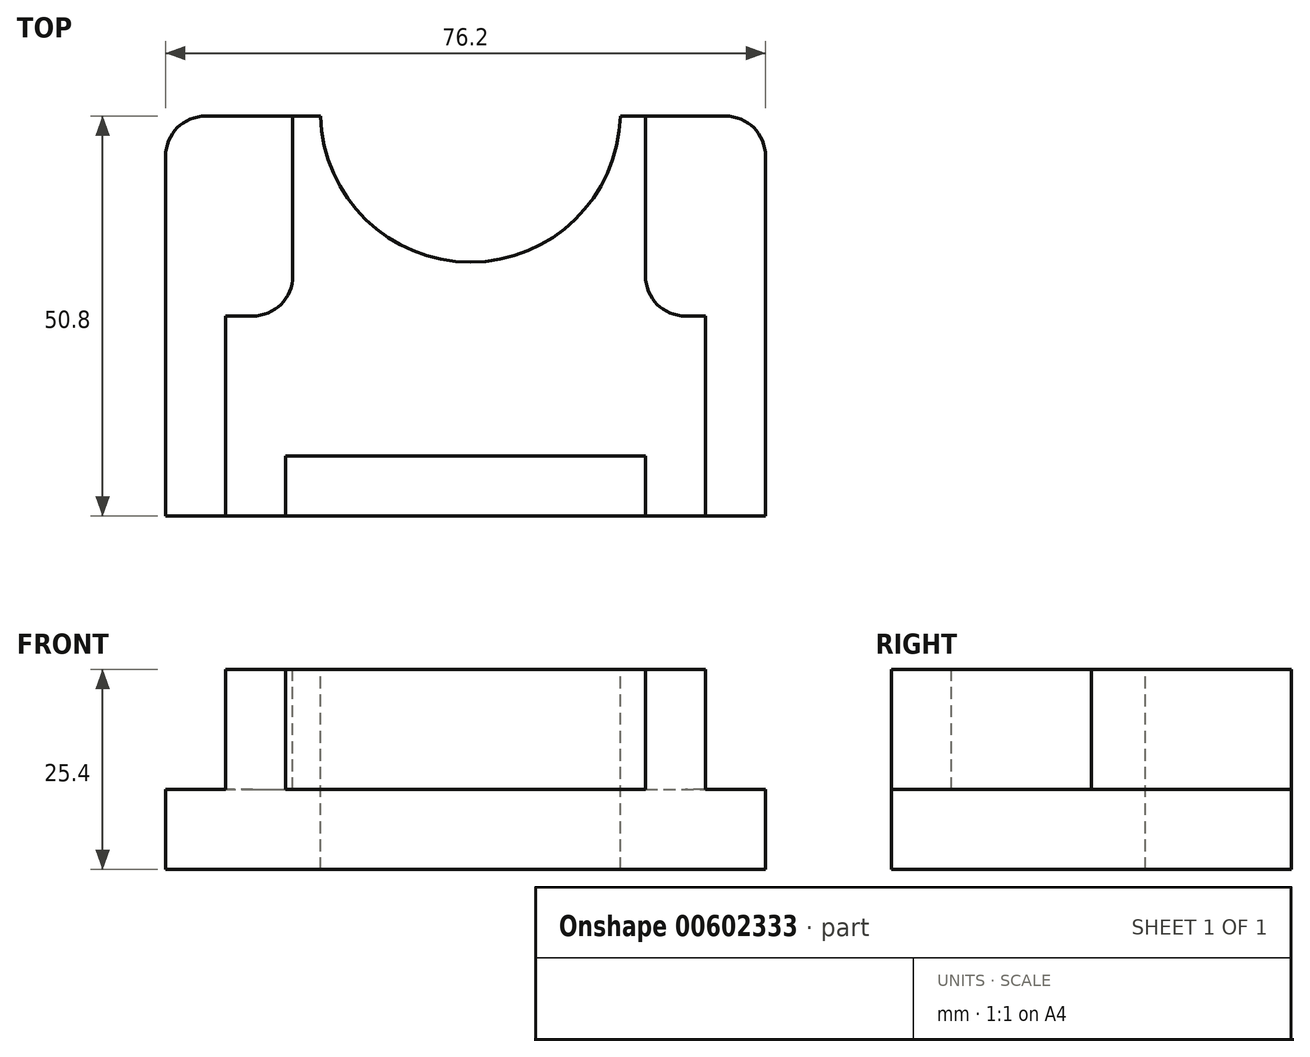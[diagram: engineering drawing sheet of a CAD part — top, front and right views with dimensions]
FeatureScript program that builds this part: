
annotation { "Feature Type Name" : "Feature", "Feature Type Description" : "" }
export const myFeature = defineFeature(function(context is Context, id is Id, definition is map)
    precondition{}
    {
        {
            var Q0;
            Q0=qCreatedBy(makeId("Top.planeOp"),FACE);
            var sketch = newSketch(context, id + "F0", { "sketchPlane" : qUnion([Q0])});
            skLineSegment(sketch, "E0.bottom", {"start": v(-50.23, 50.8) * mm, "end": v(25.97, 50.8) * mm});
            skLineSegment(sketch, "E0.top", {"start": v(-50.23, 0) * mm, "end": v(25.97, 0) * mm});
            skLineSegment(sketch, "E0.left", {"start": v(-50.23, 50.8) * mm, "end": v(-50.23, 0) * mm});
            skLineSegment(sketch, "E0.right", {"start": v(25.97, 50.8) * mm, "end": v(25.97, 0) * mm});
            skSolve(sketch);
        }
        {
            var Q0;
            Q0=makeQuery(id+"F0.imprint","IMPRINT",FACE,{"disambiguationData":[TD([[makeQuery(id+"F0.imprint","IMPRINT",EDGE,{"derivedFrom":sQuery(id+"F0.wireOp",EDGE,"E0.bottom")}),-1.0]])]});
            extrude(context, id + "F1", {"entities" : qUnion([Q0]), "depth" : 10.16 * mm, "offsetDistance" : 25.4 * mm});
        }
        {
            var Q0;
            Q0=qCreatedBy(makeId("Top.planeOp"),FACE);
            var sketch = newSketch(context, id + "F2", { "sketchPlane" : qUnion([Q0])});
            skLineSegment(sketch, "E1.bottom", {"start": v(-42.61, 50.8) * mm, "end": v(18.35, 50.8) * mm});
            skLineSegment(sketch, "E1.top", {"start": v(-42.61, 0) * mm, "end": v(18.35, 0) * mm});
            skLineSegment(sketch, "E1.left", {"start": v(-42.61, 50.8) * mm, "end": v(-42.61, 0) * mm});
            skLineSegment(sketch, "E1.right", {"start": v(18.35, 50.8) * mm, "end": v(18.35, 0) * mm});
            skSolve(sketch);
        }
        {
            var Q0;
            Q0 = qSketchRegion(id + "F2", true);
            extrude(context, id + "F3", {"entities" : qUnion([Q0]), "operationType" : NewBodyOperationType.ADD, "depth" : 25.4 * mm, "offsetDistance" : 25.4 * mm});
        }
        {
            var Q0;
            Q0=makeQuery(id+"F3.opExtrude","CAP_FACE",FACE,{"disambiguationData":[OSD([sQuery(id+"F2.wireOp",EDGE,"E1.bottom"),sQuery(id+"F2.wireOp",EDGE,"E1.top"),sQuery(id+"F2.wireOp",EDGE,"E1.left"),sQuery(id+"F2.wireOp",EDGE,"E1.right")])],"isStart":false});
            var sketch = newSketch(context, id + "F4", { "sketchPlane" : qUnion([Q0])});
            skLineSegment(sketch, "E2.bottom", {"start": v(-35, 7.62) * mm, "end": v(10.73, 7.62) * mm});
            skLineSegment(sketch, "E2.top", {"start": v(-35, 0) * mm, "end": v(10.73, 0) * mm});
            skLineSegment(sketch, "E2.left", {"start": v(-35, 7.62) * mm, "end": v(-35, 0) * mm});
            skLineSegment(sketch, "E2.right", {"start": v(10.73, 7.62) * mm, "end": v(10.73, 0) * mm});
            skCircle(sketch, "E3", {"center": v(-11.51, 51.3) * mm, "radius": 19.05 * mm});
            skLineSegment(sketch, "E4.bottom", {"start": v(-42.61, 25.4) * mm, "end": v(-34.1, 25.4) * mm});
            skLineSegment(sketch, "E4.top", {"start": v(-42.61, 50.8) * mm, "end": v(-34.1, 50.8) * mm});
            skLineSegment(sketch, "E4.left", {"start": v(-42.61, 25.4) * mm, "end": v(-42.61, 50.8) * mm});
            skLineSegment(sketch, "E4.right", {"start": v(-34.1, 25.4) * mm, "end": v(-34.1, 50.8) * mm});
            skLineSegment(sketch, "E5.bottom", {"start": v(10.73, 25.4) * mm, "end": v(18.35, 25.4) * mm});
            skLineSegment(sketch, "E5.top", {"start": v(10.73, 50.8) * mm, "end": v(18.35, 50.8) * mm});
            skLineSegment(sketch, "E5.left", {"start": v(10.73, 25.4) * mm, "end": v(10.73, 50.8) * mm});
            skLineSegment(sketch, "E5.right", {"start": v(18.35, 25.4) * mm, "end": v(18.35, 50.8) * mm});
            skSolve(sketch);
        }
        {
            var Q0;
            Q0=makeQuery(id+"F4.imprint","IMPRINT",FACE,{"disambiguationData":[TD([[makeQuery(id+"F4.imprint","IMPRINT",EDGE,{"derivedFrom":sQuery(id+"F4.wireOp",EDGE,"E3")}),1.0]])]});
            extrude(context, id + "F5", {"entities" : qUnion([Q0]), "operationType" : NewBodyOperationType.REMOVE, "endBound" : BoundingType.THROUGH_ALL, "oppositeDirection" : true, "depth" : 25.4 * mm, "offsetDistance" : 25.4 * mm});
        }
        {
            var Q0;
            Q0=makeQuery(id+"F4.imprint","IMPRINT",FACE,{"disambiguationData":[TD([[makeQuery(id+"F4.imprint","IMPRINT",EDGE,{"derivedFrom":sQuery(id+"F4.wireOp",EDGE,"E4.bottom")}),1.0]])]});
            var Q1;
            Q1=makeQuery(id+"F4.imprint","IMPRINT",FACE,{"disambiguationData":[TD([[makeQuery(id+"F4.imprint","IMPRINT",EDGE,{"derivedFrom":sQuery(id+"F4.wireOp",EDGE,"E5.bottom")}),1.0]])]});
            var Q2;
            Q2=makeQuery(id+"F4.imprint","IMPRINT",FACE,{"disambiguationData":[TD([[makeQuery(id+"F4.imprint","IMPRINT",EDGE,{"derivedFrom":sQuery(id+"F4.wireOp",EDGE,"E2.bottom")}),-1.0]])]});
            var Q3;
            {var subQ0=sQuery(id+"F0.wireOp",EDGE,"E0.top");var subQ1=sQuery(id+"F0.wireOp",EDGE,"E0.right");var subQ2=sQuery(id+"F0.wireOp",EDGE,"E0.bottom");Q3=makeQuery(id+"F3.boolean.opBoolean","SPLIT",FACE,{"disambiguationData":[TD([makeQuery(id+"F1.opExtrude","SWEPT_FACE",FACE,{"disambiguationData":[OSD([subQ1])]})])],"derivedFrom":makeQuery(id+"F1.opExtrude","CAP_FACE",FACE,{"disambiguationData":[OSD([subQ2,subQ0,sQuery(id+"F0.wireOp",EDGE,"E0.left"),subQ1])],"isStart":false})});}
            extrude(context, id + "F6", {"entities" : qUnion([Q0, Q1, Q2]), "operationType" : NewBodyOperationType.REMOVE, "endBound" : BoundingType.UP_TO_SURFACE, "oppositeDirection" : true, "depth" : 25.4 * mm, "endBoundEntityFace" : qUnion([Q3]), "offsetDistance" : 25.4 * mm, "offsetOppositeDirection" : true});
        }
        {
            var Q0;
            Q0=makeQuery(id+"F1.opExtrude","SWEPT_EDGE",EDGE,{"disambiguationData":[OSD([sQuery(id+"F0.wireOp",EDGE,"E0.bottom"),sQuery(id+"F0.wireOp",EDGE,"E0.left")])]});
            fillet(context, id + "F7", {"entities" : qUnion([Q0]), "radius" : 5.08 * mm, "tangentPropagation" : true, "allowEdgeOverflow" : false});
        }
        {
            var Q0;
            Q0=makeQuery(id+"F1.opExtrude","SWEPT_EDGE",EDGE,{"disambiguationData":[OSD([sQuery(id+"F0.wireOp",EDGE,"E0.bottom"),sQuery(id+"F0.wireOp",EDGE,"E0.right")])]});
            fillet(context, id + "F8", {"entities" : qUnion([Q0]), "radius" : 5.08 * mm, "tangentPropagation" : true, "allowEdgeOverflow" : false});
        }
        {
            var Q0;
            Q0=makeQuery(id+"F6.boolean.opBoolean","COPY",EDGE,{"derivedFrom":makeQuery(id+"F6.opExtrude","SWEPT_EDGE",EDGE,{"disambiguationData":[OSD([sQuery(id+"F4.wireOp",EDGE,"E4.bottom"),sQuery(id+"F4.wireOp",EDGE,"E4.right")])]})});
            var Q1;
            Q1=makeQuery(id+"F6.boolean.opBoolean","COPY",EDGE,{"derivedFrom":makeQuery(id+"F6.opExtrude","SWEPT_EDGE",EDGE,{"disambiguationData":[OSD([sQuery(id+"F4.wireOp",EDGE,"E5.bottom"),sQuery(id+"F4.wireOp",EDGE,"E5.left")])]})});
            fillet(context, id + "F9", {"entities" : qUnion([Q0, Q1]), "radius" : 5.08 * mm, "tangentPropagation" : true, "allowEdgeOverflow" : false});
        }
    });
